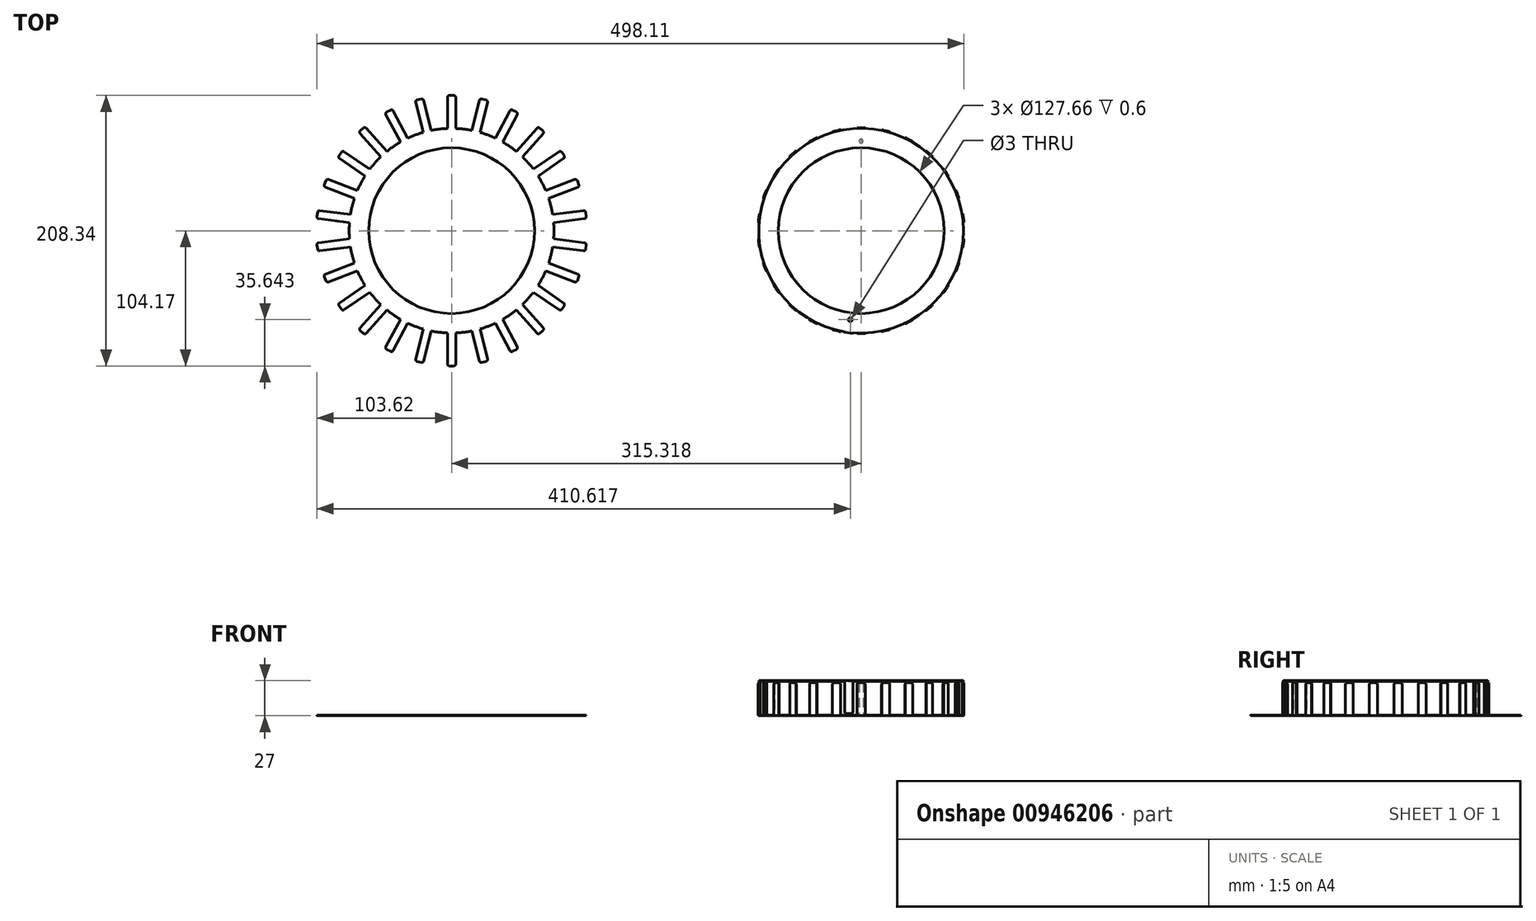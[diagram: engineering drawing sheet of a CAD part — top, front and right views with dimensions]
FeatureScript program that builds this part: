
annotation { "Feature Type Name" : "Feature", "Feature Type Description" : "" }
export const myFeature = defineFeature(function(context is Context, id is Id, definition is map)
    precondition{}
    {
        {
            assignVariable(context, id + "F0", {"name" : "NumFingers", "anyValue" : 26});
        }
        {
            var Q0;
            Q0=qCreatedBy(makeId("Top.planeOp"),FACE);
            var sketch = newSketch(context, id + "F1", { "sketchPlane" : qUnion([Q0])});
            skLineSegment(sketch, "E0", {"start": v(0, 0) * mm, "end": v(0, 78.77) * mm, "construction": true});
            skPoint(sketch, "E1.center", {"position": v(0, 0) * mm});
            skLineSegment(sketch, "E2.bottom", {"start": v(1.67, 104.17) * mm, "end": v(-1.67, 104.17) * mm});
            skLineSegment(sketch, "E2.top", {"start": v(3.17, 78.77) * mm, "end": v(-3.17, 78.77) * mm, "construction": true});
            skLineSegment(sketch, "E2.left", {"start": v(3.18, 102.67) * mm, "end": v(3.18, 78.77) * mm});
            skLineSegment(sketch, "E2.right", {"start": v(-3.17, 102.67) * mm, "end": v(-3.17, 78.77) * mm});
            skPoint(sketch, "E3", {"position": v(0, 78.77) * mm});
            skLineSegment(sketch, "E4", {"start": v(-3.18, 78.77) * mm, "end": v(0, 0) * mm, "construction": true});
            skArc(sketch, "E5", {"start": v(-3.18, 78.77) * mm, "mid": v(0, -78.83) * mm, "end": v(3.17, 78.77) * mm});
            skPoint(sketch, "E6.visualSharp", {"position": v(-3.17, 104.17) * mm});
            skArc(sketch, "E6.filletArc", {"start": v(-1.67, 104.17) * mm, "mid": v(-2.74, 103.73) * mm, "end": v(-3.17, 102.67) * mm});
            skPoint(sketch, "E7.visualSharp", {"position": v(3.17, 104.17) * mm});
            skArc(sketch, "E7.filletArc", {"start": v(3.17, 102.67) * mm, "mid": v(2.74, 103.73) * mm, "end": v(1.67, 104.17) * mm});
            skCircle(sketch, "E8", {"center": v(0, 0) * mm, "radius": 63.83 * mm});
            skSolve(sketch);
        }
        {
            var Q0;
            Q0=makeQuery(id+"F1.imprint","IMPRINT",FACE,{"disambiguationData":[TD([[makeQuery(id+"F1.imprint","IMPRINT",EDGE,{"derivedFrom":sQuery(id+"F1.wireOp",EDGE,"E2.bottom")}),1.0]])]});
            var Q1;
            {var subQ0=sQuery(id+"F1.wireOp",EDGE,"E2.top");Q1=makeQuery(id+"F1.imprint","IMPRINT",FACE,{"disambiguationData":[TD([[makeQuery(id+"F1.imprint","IMPRINT",EDGE,{"derivedFrom":subQ0}),1.0]])]});}
            var Q2;
            Q2=sQuery(id+"F1.wireOp",EDGE,"hmrcqJ3q-lU7G-KxSF-X1eN-bNX01pqxhZci");
            var Q3;
            Q3=sQuery(id+"F1.wireOp",EDGE,"hotj8Gxh-6EDq-oSzS-3hbz-jsD0qoGDDY39");
            extrude(context, id + "F2", {"entities" : qUnion([Q0, Q1]), "surfaceEntities" : qUnion([Q2, Q3]), "depth" : .6 * mm});
        }
        {
            var Q0;
            Q0=qCreatedBy(makeId("Right.planeOp"),FACE);
            var sketch = newSketch(context, id + "F3", { "sketchPlane" : qUnion([Q0])});
            skLineSegment(sketch, "E9", {"start": v(0, 49.5) * mm, "end": v(0, -49.5) * mm, "construction": true});
            skSolve(sketch);
        }
        {
            var Q0;
            Q0=makeQuery(id+"F2.opExtrude","SWEPT_BODY",BODY,{"disambiguationData":[OSD([sQuery(id+"F1.wireOp",EDGE,"E2.bottom"),sQuery(id+"F1.wireOp",EDGE,"E2.top"),sQuery(id+"F1.wireOp",EDGE,"E2.left"),sQuery(id+"F1.wireOp",EDGE,"E2.right")])]});
            var Q1;
            Q1=sQuery(id+"F3.wireOp",EDGE,"E9");
            circularPattern(context, id + "F4", {"operationType" : NewBodyOperationType.ADD, "entities" : qUnion([Q0]), "axis" : qUnion([Q1]), "angle" : 360 * degree, "instanceCount" : getVariable(context, 'NumFingers'), "equalSpace" : true});
        }
        {
            var Q0;
            Q0=qCreatedBy(makeId("Top.planeOp"),FACE);
            var sketch = newSketch(context, id + "F5", { "sketchPlane" : qUnion([Q0])});
            skLineSegment(sketch, "E10", {"start": v(315.32, 0) * mm, "end": v(315.32, 78.77) * mm, "construction": true});
            skPoint(sketch, "E11.center", {"position": v(315.32, 0) * mm});
            skLineSegment(sketch, "E12.bottom", {"start": v(318.5, 79.37) * mm, "end": v(312.14, 79.37) * mm});
            skLineSegment(sketch, "E12.top", {"start": v(318.5, 78.77) * mm, "end": v(312.14, 78.77) * mm, "construction": true});
            skLineSegment(sketch, "E12.left", {"start": v(318.5, 79.37) * mm, "end": v(318.5, 78.77) * mm});
            skLineSegment(sketch, "E12.right", {"start": v(312.14, 79.37) * mm, "end": v(312.14, 78.77) * mm});
            skPoint(sketch, "E13", {"position": v(315.32, 78.77) * mm});
            skLineSegment(sketch, "E14", {"start": v(312.14, 78.77) * mm, "end": v(315.32, 0) * mm, "construction": true});
            skArc(sketch, "E15", {"start": v(312.14, 78.77) * mm, "mid": v(315.32, -78.83) * mm, "end": v(318.5, 78.77) * mm});
            skPoint(sketch, "E16.visualSharp", {"position": v(312.14, 79.37) * mm});
            skCircle(sketch, "E17", {"center": v(315.32, 0) * mm, "radius": 63.83 * mm});
            skLineSegment(sketch, "E18", {"start": v(0, 0) * mm, "end": v(315.32, 0) * mm, "construction": true});
            skLineSegment(sketch, "E19", {"start": v(318.5, 78.77) * mm, "end": v(312.14, 78.77) * mm});
            skCircle(sketch, "E20", {"center": v(315.32, 69.03) * mm, "radius": 1.5 * mm});
            skSolve(sketch);
        }
        {
            var Q0;
            Q0=makeQuery(id+"F5.imprint","IMPRINT",FACE,{"disambiguationData":[TD([[makeQuery(id+"F5.imprint","IMPRINT",EDGE,{"derivedFrom":sQuery(id+"F5.wireOp",EDGE,"E15")}),1.0]])]});
            extrude(context, id + "F6", {"entities" : qUnion([Q0]), "depth" : 0.6 * mm});
        }
        {
            var Q0;
            Q0=makeQuery(id+"F5.imprint","IMPRINT",FACE,{"disambiguationData":[TD([[makeQuery(id+"F5.imprint","IMPRINT",EDGE,{"derivedFrom":sQuery(id+"F5.wireOp",EDGE,"E12.bottom")}),1.0]])]});
            extrude(context, id + "F7", {"entities" : qUnion([Q0]), "operationType" : NewBodyOperationType.ADD, "depth" : 25.4 * mm});
        }
        {
            var Q0;
            Q0=makeQuery(id+"F7.opExtrude","CAP_EDGE",EDGE,{"disambiguationData":[OSD([sQuery(id+"F5.wireOp",EDGE,"E12.right")])],"isStart":false});
            var Q1;
            Q1=makeQuery(id+"F7.opExtrude","CAP_EDGE",EDGE,{"disambiguationData":[OSD([sQuery(id+"F5.wireOp",EDGE,"E12.left")])],"isStart":false});
            fillet(context, id + "F8", {"entities" : qUnion([Q0, Q1]), "radius" : 1.5 * mm, "tangentPropagation" : true, "allowEdgeOverflow" : false});
        }
        {
            var Q0;
            Q0=makeQuery(id+"F7.opExtrude","CAP_EDGE",EDGE,{"disambiguationData":[OSD([sQuery(id+"F5.wireOp",EDGE,"E12.bottom")])],"isStart":true});
            fillet(context, id + "F9", {"entities" : qUnion([Q0]), "radius" : .6 * mm, "tangentPropagation" : true, "allowEdgeOverflow" : false});
        }
        {
            var Q0;
            Q0=makeQuery(id+"F7.opExtrude","CAP_EDGE",EDGE,{"disambiguationData":[OSD([sQuery(id+"F5.wireOp",EDGE,"E19")])],"isStart":false});
            cPoint(context, id + "F10", {"entities" : qUnion([Q0]), "parameter" : 0.5});
        }
        {
            var Q0;
            Q0=sQuery(id+"F5.wireOp",EDGE,"E10");
            var Q1;
            Q1=qCreatedBy(id+"F10",VERTEX);
            cPlane(context, id + "F11", {"entities" : qUnion([Q0, Q1]), "cplaneType" : CPlaneType.LINE_ANGLE, "offset" : 25 * mm, "angle" : 0 * degree, "width" : 150 * mm, "height" : 150 * mm});
        }
        {
            var Q0;
            Q0=qCreatedBy(id+"F11.planeOp",FACE);
            var sketch = newSketch(context, id + "F12", { "sketchPlane" : qUnion([Q0])});
            skLineSegment(sketch, "E21", {"start": v(0, -117.76) * mm, "end": v(0, 117.76) * mm, "construction": true});
            skPoint(sketch, "E22", {"position": v(0, 0) * mm});
            skSolve(sketch);
        }
        {
            var Q0;
            Q0=makeQuery(id+"F6.opExtrude","SWEPT_BODY",BODY,{"disambiguationData":[OSD([sQuery(id+"F5.wireOp",EDGE,"E15"),sQuery(id+"F5.wireOp",EDGE,"E17"),sQuery(id+"F5.wireOp",EDGE,"E19")])]});
            var Q1;
            Q1=sQuery(id+"F12.wireOp",EDGE,"E21");
            circularPattern(context, id + "F13", {"operationType" : NewBodyOperationType.ADD, "entities" : qUnion([Q0]), "axis" : qUnion([Q1]), "angle" : 360 * degree, "instanceCount" : getVariable(context, 'NumFingers'), "equalSpace" : true});
        }
        {
            var Q0;
            Q0=makeQuery(id+"F6.opExtrude","SWEPT_BODY",BODY,{"disambiguationData":[OSD([sQuery(id+"F5.wireOp",EDGE,"E15"),sQuery(id+"F5.wireOp",EDGE,"E17"),sQuery(id+"F5.wireOp",EDGE,"E19")])]});
            var Q1;
            Q1=makeQuery(id+"F6.opExtrude","CAP_EDGE",EDGE,{"disambiguationData":[OSD([sQuery(id+"F5.wireOp",EDGE,"E17")])],"isStart":false});
            transform(context, id + "F14", {"entities" : qUnion([Q0]), "transformType" : TransformType.ROTATION, "transformAxis" : qUnion([Q1]), "angle" : (180 / getVariable(context, 'NumFingers')) * degree, "makeCopy" : true});
        }
        {
            var Q0;
            Q0=makeQuery(id+"F14.opPattern","COPY",BODY,{"derivedFrom":makeQuery(id+"F6.opExtrude","SWEPT_BODY",BODY,{"disambiguationData":[OSD([sQuery(id+"F5.wireOp",EDGE,"E15"),sQuery(id+"F5.wireOp",EDGE,"E17"),sQuery(id+"F5.wireOp",EDGE,"E19")])]}),"instanceName":"1"});
            var Q1;
            Q1=sQuery(id+"F5.wireOp",EDGE,"E18");
            transform(context, id + "F15", {"entities" : qUnion([Q0]), "transformType" : TransformType.ROTATION, "transformAxis" : qUnion([Q1]), "angle" : 180 * degree, "makeCopy" : false});
        }
        {
            var Q0;
            Q0=makeQuery(id+"F14.opPattern","COPY",BODY,{"derivedFrom":makeQuery(id+"F6.opExtrude","SWEPT_BODY",BODY,{"disambiguationData":[OSD([sQuery(id+"F5.wireOp",EDGE,"E15"),sQuery(id+"F5.wireOp",EDGE,"E17"),sQuery(id+"F5.wireOp",EDGE,"E19")])]}),"instanceName":"1"});
            var Q1;
            Q1=sQuery(id+"F12.wireOp",EDGE,"E21");
            transform(context, id + "F16", {"entities" : qUnion([Q0]), "transformType" : TransformType.TRANSLATION_DISTANCE, "transformDirection" : qUnion([Q1]), "distance" : 27 * mm, "makeCopy" : false});
        }
        {
            var Q0;
            Q0=makeQuery(id+"F5.imprint","IMPRINT",FACE,{"disambiguationData":[TD([[makeQuery(id+"F5.imprint","IMPRINT",EDGE,{"derivedFrom":sQuery(id+"F5.wireOp",EDGE,"E20")}),1.0]])]});
            var Q1;
            {var subQ0=makeQuery(id+"F6.opExtrude","CAP_FACE",FACE,{"disambiguationData":[OSD([sQuery(id+"F5.wireOp",EDGE,"E15"),sQuery(id+"F5.wireOp",EDGE,"E17"),sQuery(id+"F5.wireOp",EDGE,"E19"),sQuery(id+"F5.wireOp",EDGE,"E20")])],"isStart":false});Q1=makeQuery(id+"F14.opPattern","COPY",FACE,{"derivedFrom":makeQuery(id+"F13.boolean.opBoolean","MERGE",FACE,{"derivedFrom":[subQ0,makeQuery(id+"F13.opPattern","COPY",FACE,{"derivedFrom":subQ0,"instanceName":"1"}),makeQuery(id+"F13.opPattern","COPY",FACE,{"derivedFrom":subQ0,"instanceName":"2"}),makeQuery(id+"F13.opPattern","COPY",FACE,{"derivedFrom":subQ0,"instanceName":"3"}),makeQuery(id+"F13.opPattern","COPY",FACE,{"derivedFrom":subQ0,"instanceName":"4"}),makeQuery(id+"F13.opPattern","COPY",FACE,{"derivedFrom":subQ0,"instanceName":"5"}),makeQuery(id+"F13.opPattern","COPY",FACE,{"derivedFrom":subQ0,"instanceName":"6"}),makeQuery(id+"F13.opPattern","COPY",FACE,{"derivedFrom":subQ0,"instanceName":"7"}),makeQuery(id+"F13.opPattern","COPY",FACE,{"derivedFrom":subQ0,"instanceName":"8"}),makeQuery(id+"F13.opPattern","COPY",FACE,{"derivedFrom":subQ0,"instanceName":"9"}),makeQuery(id+"F13.opPattern","COPY",FACE,{"derivedFrom":subQ0,"instanceName":"10"}),makeQuery(id+"F13.opPattern","COPY",FACE,{"derivedFrom":subQ0,"instanceName":"11"}),makeQuery(id+"F13.opPattern","COPY",FACE,{"derivedFrom":subQ0,"instanceName":"12"}),makeQuery(id+"F13.opPattern","COPY",FACE,{"derivedFrom":subQ0,"instanceName":"13"}),makeQuery(id+"F13.opPattern","COPY",FACE,{"derivedFrom":subQ0,"instanceName":"14"}),makeQuery(id+"F13.opPattern","COPY",FACE,{"derivedFrom":subQ0,"instanceName":"15"}),makeQuery(id+"F13.opPattern","COPY",FACE,{"derivedFrom":subQ0,"instanceName":"16"}),makeQuery(id+"F13.opPattern","COPY",FACE,{"derivedFrom":subQ0,"instanceName":"17"}),makeQuery(id+"F13.opPattern","COPY",FACE,{"derivedFrom":subQ0,"instanceName":"18"}),makeQuery(id+"F13.opPattern","COPY",FACE,{"derivedFrom":subQ0,"instanceName":"19"}),makeQuery(id+"F13.opPattern","COPY",FACE,{"derivedFrom":subQ0,"instanceName":"20"}),makeQuery(id+"F13.opPattern","COPY",FACE,{"derivedFrom":subQ0,"instanceName":"21"}),makeQuery(id+"F13.opPattern","COPY",FACE,{"derivedFrom":subQ0,"instanceName":"22"}),makeQuery(id+"F13.opPattern","COPY",FACE,{"derivedFrom":subQ0,"instanceName":"23"}),makeQuery(id+"F13.opPattern","COPY",FACE,{"derivedFrom":subQ0,"instanceName":"24"}),makeQuery(id+"F13.opPattern","COPY",FACE,{"derivedFrom":subQ0,"instanceName":"25"}),makeQuery(id+"F13.opPattern","COPY",FACE,{"derivedFrom":subQ0,"instanceName":"26"}),makeQuery(id+"F13.opPattern","COPY",FACE,{"derivedFrom":subQ0,"instanceName":"27"}),makeQuery(id+"F13.opPattern","COPY",FACE,{"derivedFrom":subQ0,"instanceName":"28"}),makeQuery(id+"F13.opPattern","COPY",FACE,{"derivedFrom":subQ0,"instanceName":"29"}),makeQuery(id+"F13.opPattern","COPY",FACE,{"derivedFrom":subQ0,"instanceName":"30"}),makeQuery(id+"F13.opPattern","COPY",FACE,{"derivedFrom":subQ0,"instanceName":"31"})]}),"instanceName":"1"});}
            extrude(context, id + "F17", {"entities" : qUnion([Q0]), "operationType" : NewBodyOperationType.ADD, "endBound" : BoundingType.UP_TO_SURFACE, "endBoundEntityFace" : qUnion([Q1]), "depth" : 25 * mm});
        }
    });
